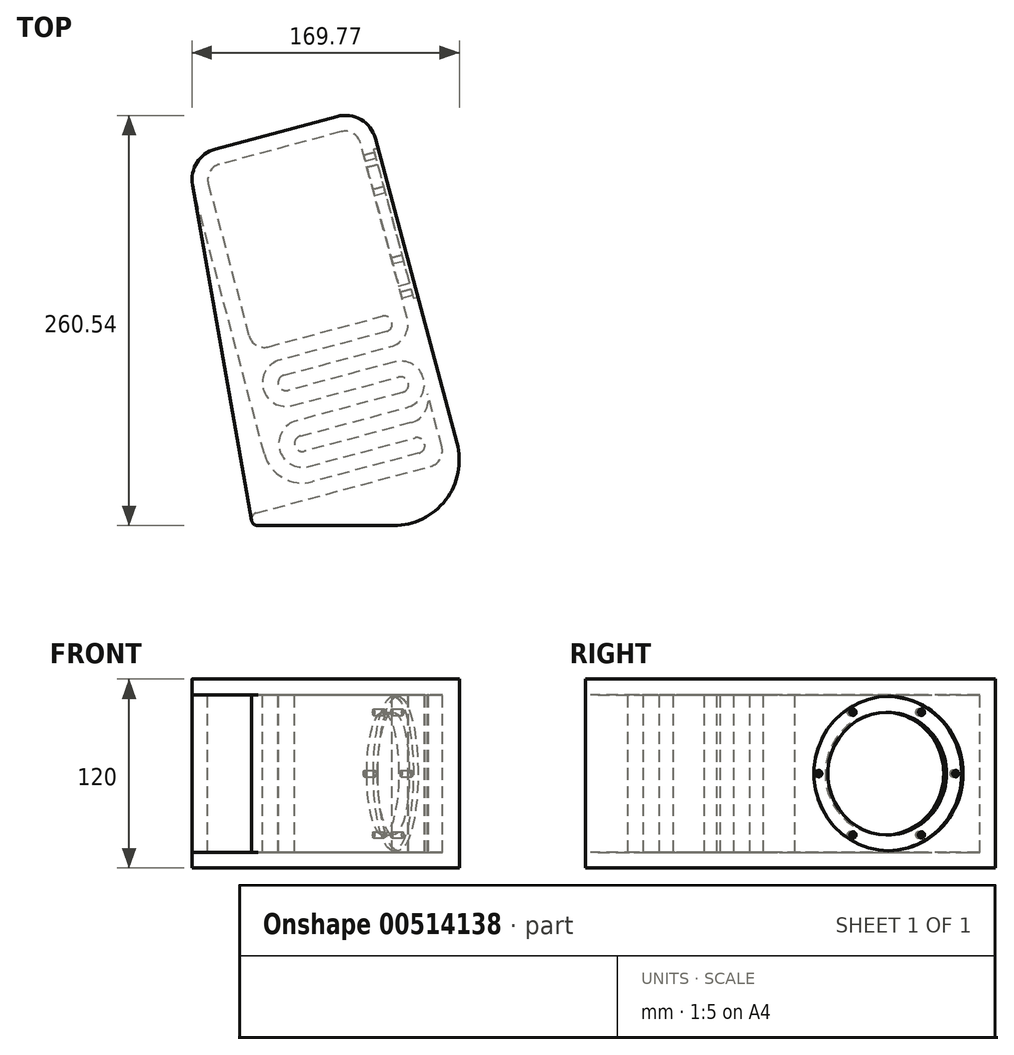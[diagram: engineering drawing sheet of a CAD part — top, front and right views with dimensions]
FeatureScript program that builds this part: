
annotation { "Feature Type Name" : "Feature", "Feature Type Description" : "" }
export const myFeature = defineFeature(function(context is Context, id is Id, definition is map)
    precondition{}
    {
        {
            var Q0;
            Q0=qCreatedBy(makeId("Top.planeOp"),FACE);
            var sketch = newSketch(context, id + "F0", { "sketchPlane" : qUnion([Q0])});
            skLineSegment(sketch, "E0", {"start": v(-51.3, -194.92) * mm, "end": v(-96.6, -25.88) * mm});
            skArc(sketch, "E1", {"start": v(-96.6, -25.88) * mm, "mid": v(-94.6, -10.7) * mm, "end": v(-82.45, -1.39) * mm});
            skLineSegment(sketch, "E2", {"start": v(-82.45, -1.39) * mm, "end": v(-5.18, 19.32) * mm});
            skArc(sketch, "E3", {"start": v(-5.18, 19.32) * mm, "mid": v(10, 17.32) * mm, "end": v(19.32, 5.18) * mm});
            skLineSegment(sketch, "E4", {"start": v(19.32, 5.18) * mm, "end": v(71.08, -188) * mm});
            skArc(sketch, "E5", {"start": v(71.08, -188) * mm, "mid": v(63.88, -224.21) * mm, "end": v(30.78, -240.54) * mm});
            skLineSegment(sketch, "E6", {"start": v(30.78, -240.54) * mm, "end": v(-55.4, -240.54) * mm});
            skArc(sketch, "E7", {"start": v(-55.4, -240.54) * mm, "mid": v(-59.44, -237) * mm, "end": v(-56.46, -232.54) * mm});
            skLineSegment(sketch, "E8", {"start": v(-56.46, -232.54) * mm, "end": v(54.35, -202.84) * mm});
            skArc(sketch, "E9", {"start": v(54.35, -202.84) * mm, "mid": v(60.42, -198.19) * mm, "end": v(61.42, -190.6) * mm});
            skLineSegment(sketch, "E10", {"start": v(61.42, -190.6) * mm, "end": v(52.36, -156.79) * mm});
            skArc(sketch, "E11", {"start": v(52.36, -156.79) * mm, "mid": v(50.87, -168.17) * mm, "end": v(41.76, -175.16) * mm});
            skLineSegment(sketch, "E12", {"start": v(41.76, -175.16) * mm, "end": v(-25.86, -193.28) * mm});
            skArc(sketch, "E13", {"start": v(-25.86, -193.28) * mm, "mid": v(-31.98, -189.74) * mm, "end": v(-28.45, -183.62) * mm});
            skLineSegment(sketch, "E14", {"start": v(-28.45, -183.62) * mm, "end": v(39.17, -165.5) * mm});
            skLineSegment(sketch, "E15", {"start": v(31.4, -136.52) * mm, "end": v(-36.2, -154.64) * mm});
            skLineSegment(sketch, "E16", {"start": v(-38.8, -144.98) * mm, "end": v(28.82, -126.86) * mm});
            skArc(sketch, "E17", {"start": v(28.82, -126.86) * mm, "mid": v(37.92, -119.88) * mm, "end": v(39.42, -108.5) * mm});
            skLineSegment(sketch, "E18", {"start": v(39.42, -108.5) * mm, "end": v(9.66, 2.59) * mm});
            skArc(sketch, "E19", {"start": v(9.66, 2.59) * mm, "mid": v(5, 8.66) * mm, "end": v(-2.59, 9.66) * mm});
            skLineSegment(sketch, "E20", {"start": v(-2.59, 9.66) * mm, "end": v(-79.86, -11.05) * mm});
            skArc(sketch, "E21", {"start": v(-79.86, -11.05) * mm, "mid": v(-85.93, -15.7) * mm, "end": v(-86.93, -23.3) * mm});
            skLineSegment(sketch, "E22", {"start": v(-86.93, -23.3) * mm, "end": v(-61.05, -119.89) * mm});
            skArc(sketch, "E23", {"start": v(-61.05, -119.89) * mm, "mid": v(-56.4, -125.96) * mm, "end": v(-48.8, -126.96) * mm});
            skLineSegment(sketch, "E24", {"start": v(-48.8, -126.96) * mm, "end": v(23.64, -107.55) * mm});
            skArc(sketch, "E25", {"start": v(23.64, -107.55) * mm, "mid": v(29.76, -111.08) * mm, "end": v(26.23, -117.2) * mm});
            skLineSegment(sketch, "E26", {"start": v(26.23, -117.2) * mm, "end": v(-41.39, -135.32) * mm});
            skArc(sketch, "E27", {"start": v(-41.39, -135.32) * mm, "mid": v(-52, -153.7) * mm, "end": v(-33.62, -164.3) * mm});
            skLineSegment(sketch, "E28", {"start": v(-33.62, -164.3) * mm, "end": v(34, -146.18) * mm});
            skArc(sketch, "E29", {"start": v(34, -146.18) * mm, "mid": v(40.12, -149.72) * mm, "end": v(36.58, -155.84) * mm});
            skLineSegment(sketch, "E30", {"start": v(36.58, -155.84) * mm, "end": v(-31.03, -173.96) * mm});
            skArc(sketch, "E31", {"start": v(-31.03, -173.96) * mm, "mid": v(-41.64, -192.33) * mm, "end": v(-23.27, -202.94) * mm});
            skLineSegment(sketch, "E32", {"start": v(-23.27, -202.94) * mm, "end": v(44.35, -184.82) * mm});
            skArc(sketch, "E33", {"start": v(44.35, -184.82) * mm, "mid": v(50.47, -188.36) * mm, "end": v(46.93, -194.48) * mm});
            skLineSegment(sketch, "E34", {"start": v(46.93, -194.48) * mm, "end": v(-20.68, -212.6) * mm});
            skArc(sketch, "E35", {"start": v(-20.68, -212.6) * mm, "mid": v(-39.65, -210.1) * mm, "end": v(-51.3, -194.92) * mm});
            skArc(sketch, "E36", {"start": v(31.4, -136.52) * mm, "mid": v(49.78, -147.13) * mm, "end": v(39.17, -165.5) * mm});
            skArc(sketch, "E37", {"start": v(-38.8, -144.98) * mm, "mid": v(-42.33, -151.1) * mm, "end": v(-36.2, -154.64) * mm});
            skLineSegment(sketch, "E38", {"start": v(-96.97, -24.18) * mm, "end": v(-59.41, -237.17) * mm});
            skLineSegment(sketch, "E39", {"start": v(-41.39, -135.32) * mm, "end": v(-20.68, -212.6) * mm, "construction": true});
            skLineSegment(sketch, "E40", {"start": v(23.64, -107.55) * mm, "end": v(46.93, -194.48) * mm, "construction": true});
            skSolve(sketch);
        }
        {
            var Q0;
            {var subQ4=sQuery(id+"F0.wireOp",EDGE,"E0");Q0=makeQuery(id+"F0.imprint","IMPRINT",FACE,{"disambiguationData":[TD([[makeQuery(id+"F0.imprint","IMPRINT",EDGE,{"derivedFrom":subQ4}),1.0]])]});}
            var Q1;
            {var subQ5=sQuery(id+"F0.wireOp",EDGE,"E0");Q1=makeQuery(id+"F0.imprint","IMPRINT",FACE,{"disambiguationData":[TD([[makeQuery(id+"F0.imprint","IMPRINT",EDGE,{"derivedFrom":subQ5}),-1.0]])]});}
            extrude(context, id + "F1", {"entities" : qUnion([Q0, Q1]), "endBound" : BoundingType.SYMMETRIC, "depth" : 120 * mm, "offsetDistance" : 25 * mm});
        }
        {
            var Q0;
            {var subQ4=sQuery(id+"F0.wireOp",EDGE,"E0");Q0=makeQuery(id+"F0.imprint","IMPRINT",FACE,{"disambiguationData":[TD([[makeQuery(id+"F0.imprint","IMPRINT",EDGE,{"derivedFrom":subQ4}),1.0]])]});}
            extrude(context, id + "F2", {"entities" : qUnion([Q0]), "operationType" : NewBodyOperationType.REMOVE, "endBound" : BoundingType.SYMMETRIC, "oppositeDirection" : true, "depth" : 100 * mm, "offsetDistance" : 25 * mm});
        }
        {
            var Q0;
            Q0=makeQuery(id+"F1.opExtrude","SWEPT_FACE",FACE,{"disambiguationData":[OSD([sQuery(id+"F0.wireOp",EDGE,"E4")])]});
            var sketch = newSketch(context, id + "F3", { "sketchPlane" : qUnion([Q0])});
            skPoint(sketch, "E41.0", {"position": v(-110, 0) * mm});
            skPoint(sketch, "E42.0", {"position": v(0, 0) * mm});
            skLineSegment(sketch, "E43.bottom", {"start": v(-110, 50) * mm, "end": v(0, 50) * mm});
            skLineSegment(sketch, "E43.top", {"start": v(-110, -50) * mm, "end": v(0, -50) * mm});
            skLineSegment(sketch, "E43.left", {"start": v(-110, 50) * mm, "end": v(-110, -50) * mm});
            skLineSegment(sketch, "E43.right", {"start": v(0, 50) * mm, "end": v(0, -50) * mm});
            skLineSegment(sketch, "E44", {"start": v(-110, 50) * mm, "end": v(0, -50) * mm, "construction": true});
            skLineSegment(sketch, "E45", {"start": v(-110, -50) * mm, "end": v(0, 50) * mm, "construction": true});
            skPoint(sketch, "E46", {"position": v(-55, 0) * mm});
            skCircle(sketch, "E47", {"center": v(-55, 0) * mm, "radius": 49 * mm});
            skCircle(sketch, "E48", {"center": v(-55, 0) * mm, "radius": 39 * mm});
            skPoint(sketch, "E49", {"position": v(-10, 0) * mm});
            skPoint(sketch, "E50.1.0", {"position": v(-32.5, 38.97) * mm});
            skPoint(sketch, "E50.2.0", {"position": v(-77.5, 38.97) * mm});
            skPoint(sketch, "E50.3.0", {"position": v(-100, 0) * mm});
            skPoint(sketch, "E50.4.0", {"position": v(-77.5, -38.97) * mm});
            skPoint(sketch, "E50.5.0", {"position": v(-32.5, -38.97) * mm});
            skSolve(sketch);
        }
        {
            var Q0;
            Q0=makeQuery(id+"F3.imprint","IMPRINT",FACE,{"disambiguationData":[TD([[makeQuery(id+"F3.imprint","IMPRINT",EDGE,{"derivedFrom":sQuery(id+"F3.wireOp",EDGE,"E48")}),1.0]])]});
            extrude(context, id + "F4", {"entities" : qUnion([Q0]), "operationType" : NewBodyOperationType.REMOVE, "oppositeDirection" : true, "depth" : 10 * mm, "offsetDistance" : 25 * mm});
        }
        {
            var Q0;
            Q0=makeQuery(id+"F3.imprint","IMPRINT",FACE,{"disambiguationData":[TD([[makeQuery(id+"F3.imprint","IMPRINT",EDGE,{"derivedFrom":sQuery(id+"F3.wireOp",EDGE,"E47")}),1.0]])]});
            extrude(context, id + "F5", {"entities" : qUnion([Q0]), "operationType" : NewBodyOperationType.REMOVE, "oppositeDirection" : true, "depth" : 3 * mm, "offsetDistance" : 25 * mm});
        }
        {
            var Q0;
            Q0=sQuery(id+"F3.wireOp",VERTEX,"E49");
            var Q1;
            Q1=sQuery(id+"F3.wireOp",VERTEX,"E50.5.0");
            var Q2;
            Q2=sQuery(id+"F3.wireOp",VERTEX,"E50.4.0");
            var Q3;
            Q3=sQuery(id+"F3.wireOp",VERTEX,"E50.3.0");
            var Q4;
            Q4=sQuery(id+"F3.wireOp",VERTEX,"E50.2.0");
            var Q5;
            Q5=sQuery(id+"F3.wireOp",VERTEX,"E50.1.0");
            var Q6;
            Q6=makeQuery(id+"F1.opExtrude","SWEPT_BODY",BODY,{"disambiguationData":[OSD([sQuery(id+"F0.wireOp",EDGE,"E1"),sQuery(id+"F0.wireOp",EDGE,"E2"),sQuery(id+"F0.wireOp",EDGE,"E3"),sQuery(id+"F0.wireOp",EDGE,"E4"),sQuery(id+"F0.wireOp",EDGE,"E5"),sQuery(id+"F0.wireOp",EDGE,"E6"),sQuery(id+"F0.wireOp",EDGE,"E7"),sQuery(id+"F0.wireOp",EDGE,"E38")])]});
            hole(context, id + "F6", {"style" : HoleStyle.SIMPLE, "endStyle" : HoleEndStyle.BLIND, "holeDiameter" : 4 * mm, "majorDiameter" : 5 * mm, "holeDepth" : 20 * mm, "isTappedThrough" : true, "tappedDepth" : 12 * mm, "tapClearance" : 3, "startFromSketch" : true, "locations" : qUnion([Q0, Q1, Q2, Q3, Q4, Q5]), "scope" : qUnion([Q6])});
        }
    });
